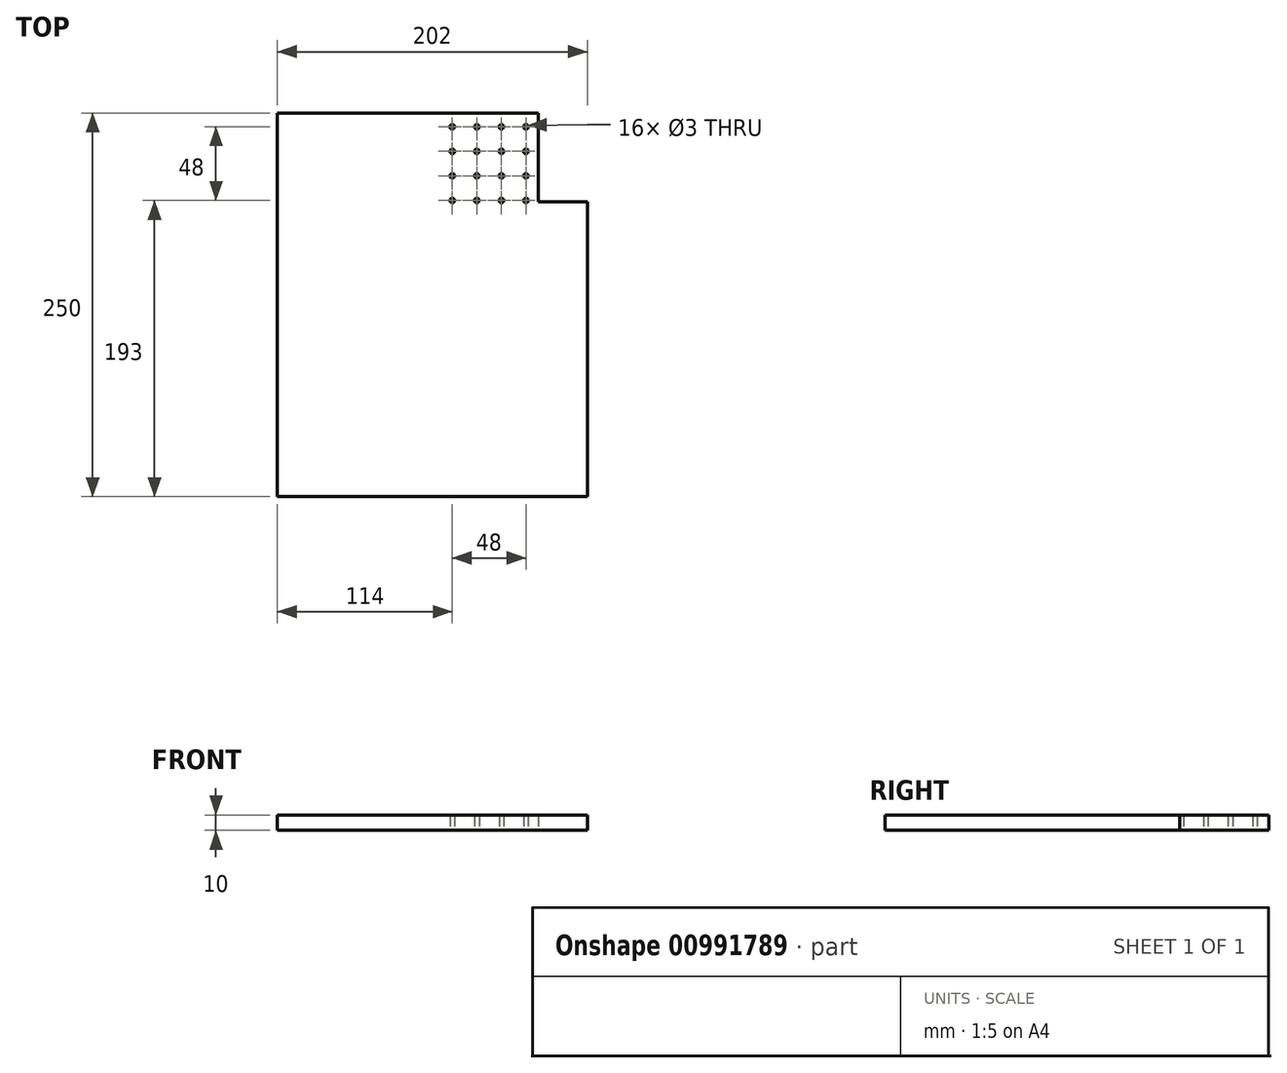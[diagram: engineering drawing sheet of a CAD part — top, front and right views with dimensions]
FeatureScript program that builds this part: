
annotation { "Feature Type Name" : "Feature", "Feature Type Description" : "" }
export const myFeature = defineFeature(function(context is Context, id is Id, definition is map)
    precondition{}
    {
        {
            var Q0;
            Q0=qCreatedBy(makeId("Top.planeOp"),FACE);
            var sketch = newSketch(context, id + "F0", { "sketchPlane" : qUnion([Q0])});
            skLineSegment(sketch, "E0", {"start": v(0, 0) * mm, "end": v(210, 0) * mm, "construction": true});
            skLineSegment(sketch, "E1.bottom", {"start": v(0, 158.5) * mm, "end": v(170, 158.5) * mm});
            skLineSegment(sketch, "E1.top", {"start": v(0, -91.5) * mm, "end": v(202, -91.5) * mm});
            skLineSegment(sketch, "E1.left", {"start": v(0, 158.5) * mm, "end": v(0, -91.5) * mm});
            skLineSegment(sketch, "E1.right", {"start": v(202, 100.5) * mm, "end": v(202, -91.5) * mm});
            skLineSegment(sketch, "E2.top", {"start": v(202, 100.5) * mm, "end": v(170, 100.5) * mm});
            skLineSegment(sketch, "E2.right", {"start": v(170, 158.5) * mm, "end": v(170, 100.5) * mm});
            skCircle(sketch, "E3", {"center": v(114, 101.5) * mm, "radius": 1.5 * mm});
            skCircle(sketch, "E4.0.1.0", {"center": v(114, 117.5) * mm, "radius": 1.5 * mm});
            skCircle(sketch, "E4.0.2.0", {"center": v(114, 133.5) * mm, "radius": 1.5 * mm});
            skCircle(sketch, "E4.0.3.0", {"center": v(114, 149.5) * mm, "radius": 1.5 * mm});
            skCircle(sketch, "E4.1.0.0", {"center": v(130, 101.5) * mm, "radius": 1.5 * mm});
            skCircle(sketch, "E4.1.1.0", {"center": v(130, 117.5) * mm, "radius": 1.5 * mm});
            skCircle(sketch, "E4.1.2.0", {"center": v(130, 133.5) * mm, "radius": 1.5 * mm});
            skCircle(sketch, "E4.1.3.0", {"center": v(130, 149.5) * mm, "radius": 1.5 * mm});
            skCircle(sketch, "E4.2.0.0", {"center": v(146, 101.5) * mm, "radius": 1.5 * mm});
            skCircle(sketch, "E4.2.1.0", {"center": v(146, 117.5) * mm, "radius": 1.5 * mm});
            skCircle(sketch, "E4.2.2.0", {"center": v(146, 133.5) * mm, "radius": 1.5 * mm});
            skCircle(sketch, "E4.2.3.0", {"center": v(146, 149.5) * mm, "radius": 1.5 * mm});
            skCircle(sketch, "E4.3.0.0", {"center": v(162, 101.5) * mm, "radius": 1.5 * mm});
            skCircle(sketch, "E4.3.1.0", {"center": v(162, 117.5) * mm, "radius": 1.5 * mm});
            skCircle(sketch, "E4.3.2.0", {"center": v(162, 133.5) * mm, "radius": 1.5 * mm});
            skCircle(sketch, "E4.3.3.0", {"center": v(162, 149.5) * mm, "radius": 1.5 * mm});
            skLineSegment(sketch, "E4.direction1", {"start": v(114, 101.5) * mm, "end": v(130, 101.5) * mm, "construction": true});
            skLineSegment(sketch, "E4.direction2", {"start": v(114, 101.5) * mm, "end": v(114, 117.5) * mm, "construction": true});
            skSolve(sketch);
        }
        {
            var Q0;
            Q0=makeQuery(id+"F0.imprint","IMPRINT",FACE,{"disambiguationData":[TD([[makeQuery(id+"F0.imprint","IMPRINT",EDGE,{"derivedFrom":sQuery(id+"F0.wireOp",EDGE,"E1.bottom")}),-1.0]])]});
            extrude(context, id + "F1", {"entities" : qUnion([Q0]), "depth" : 10 * mm, "offsetDistance" : 25 * mm});
        }
    });
